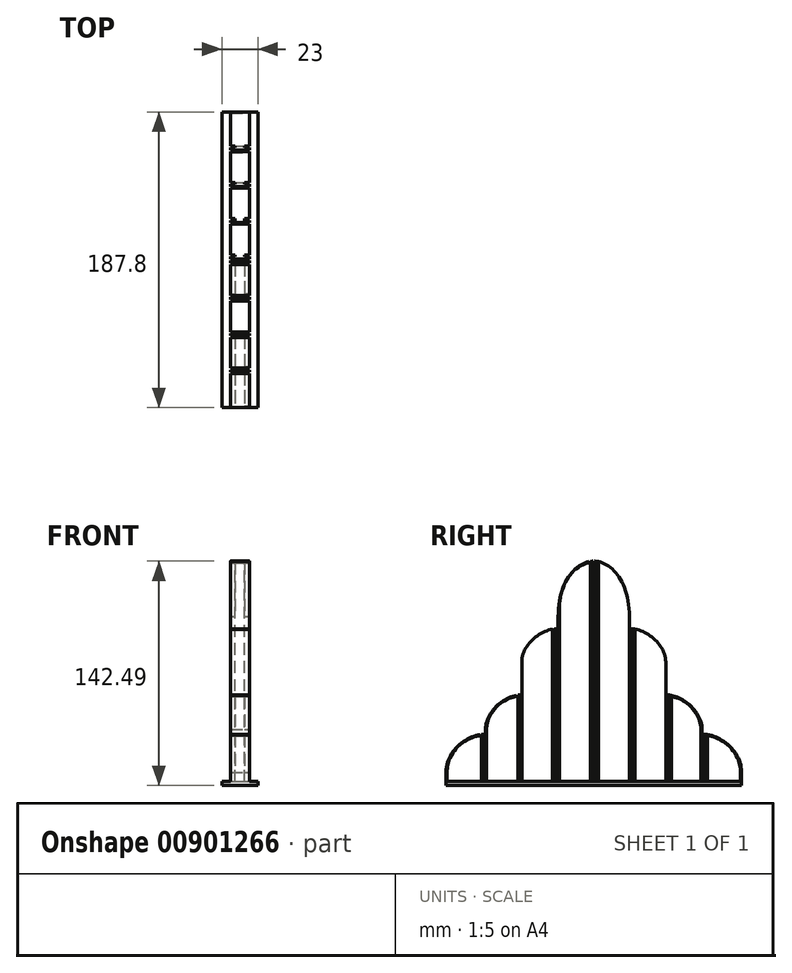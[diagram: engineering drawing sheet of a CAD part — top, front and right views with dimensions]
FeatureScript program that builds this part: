
annotation { "Feature Type Name" : "Feature", "Feature Type Description" : "" }
export const myFeature = defineFeature(function(context is Context, id is Id, definition is map)
    precondition{}
    {
        {
            var Q0;
            Q0=qCreatedBy(makeId("Right.planeOp"),FACE);
            var sketch = newSketch(context, id + "F0", { "sketchPlane" : qUnion([Q0])});
            skLineSegment(sketch, "E0", {"start": v(2, -140) * mm, "end": v(2, 0) * mm});
            skLineSegment(sketch, "E1", {"start": v(3, -140) * mm, "end": v(3, -0.3) * mm});
            skLineSegment(sketch, "E2", {"start": v(3.8, -140) * mm, "end": v(3.8, -1.32) * mm});
            skLineSegment(sketch, "E3", {"start": v(21.8, -140) * mm, "end": v(21.8, -35) * mm});
            skLineSegment(sketch, "E4", {"start": v(22.6, -140) * mm, "end": v(22.6, -35) * mm});
            skLineSegment(sketch, "E5", {"start": v(23.6, -140) * mm, "end": v(23.6, -43) * mm});
            skLineSegment(sketch, "E6", {"start": v(25.1, -140) * mm, "end": v(25.1, -43) * mm});
            skLineSegment(sketch, "E7", {"start": v(26.1, -140) * mm, "end": v(26.1, -43.2) * mm});
            skLineSegment(sketch, "E8", {"start": v(26.9, -140) * mm, "end": v(26.9, -44.15) * mm});
            skLineSegment(sketch, "E9", {"start": v(44.9, -140) * mm, "end": v(44.9, -64) * mm});
            skLineSegment(sketch, "E10", {"start": v(45.7, -140) * mm, "end": v(45.7, -64) * mm});
            skLineSegment(sketch, "E11", {"start": v(46.7, -140) * mm, "end": v(46.7, -85) * mm});
            skLineSegment(sketch, "E12", {"start": v(48.2, -140) * mm, "end": v(48.2, -85) * mm});
            skLineSegment(sketch, "E13", {"start": v(49.2, -140) * mm, "end": v(49.2, -85) * mm});
            skLineSegment(sketch, "E14", {"start": v(50, -140) * mm, "end": v(50, -86.2) * mm});
            skLineSegment(sketch, "E15", {"start": v(68, -140) * mm, "end": v(68, -107) * mm});
            skLineSegment(sketch, "E16", {"start": v(68.8, -140) * mm, "end": v(68.8, -107) * mm});
            skLineSegment(sketch, "E17", {"start": v(69.8, -140) * mm, "end": v(69.8, -110) * mm});
            skLineSegment(sketch, "E18", {"start": v(71.3, -140) * mm, "end": v(71.3, -110) * mm});
            skLineSegment(sketch, "E19", {"start": v(72.3, -140) * mm, "end": v(72.3, -110) * mm});
            skLineSegment(sketch, "E20", {"start": v(73.1, -140) * mm, "end": v(73.1, -111.15) * mm});
            skLineSegment(sketch, "E21", {"start": v(0.5, -140) * mm, "end": v(0.5, 0) * mm});
            skLineSegment(sketch, "E22", {"start": v(0, 0) * mm, "end": v(0, -140) * mm, "construction": true});
            skLineSegment(sketch, "E23", {"start": v(0, 0) * mm, "end": v(0, 21.1) * mm, "construction": true});
            skLineSegment(sketch, "E24", {"start": v(0, -140) * mm, "end": v(93.9, -140) * mm});
            skLineSegment(sketch, "E25", {"start": v(93.1, -140) * mm, "end": v(93.1, -134) * mm});
            skLineSegment(sketch, "E26", {"start": v(93.9, -140) * mm, "end": v(93.9, -134) * mm});
            skLineSegment(sketch, "E27", {"start": v(116.83, -43) * mm, "end": v(0, -43) * mm, "construction": true});
            skLineSegment(sketch, "E28", {"start": v(0, -85) * mm, "end": v(135.66, -85) * mm, "construction": true});
            skLineSegment(sketch, "E29", {"start": v(0, -110) * mm, "end": v(143.7, -110) * mm, "construction": true});
            skFitSpline(sketch, "E30", {"points": [v(69.8, -110) * mm, v(93.9, -134) * mm], "startDerivative": vector(30.93, 0) * mm, "endDerivative": vector(0, -40.3) * mm});
            skFitSpline(sketch, "E31", {"points": [v(46.7, -85) * mm, v(68.8, -107) * mm], "startDerivative": vector(29.83, 0) * mm, "endDerivative": vector(0, -33.26) * mm});
            skFitSpline(sketch, "E32", {"points": [v(23.6, -43) * mm, v(45.7, -64) * mm], "startDerivative": vector(30.98, 0) * mm, "endDerivative": vector(0, -31.98) * mm});
            skFitSpline(sketch, "E33", {"points": [v(0, 0) * mm, v(22.6, -35) * mm], "startDerivative": vector(33.21, 0) * mm, "endDerivative": vector(0, -66.82) * mm});
            skLineSegment(sketch, "E34", {"start": v(0, 0) * mm, "end": v(35.18, 0) * mm, "construction": true});
            skFitSpline(sketch, "E35.trimOffspring", {"points": [v(0, -0.8) * mm, v(1.3, -0.8) * mm, v(3.94, -1.18) * mm, v(9.13, -3.4) * mm, v(15.13, -8.92) * mm, v(20.38, -19.7) * mm, v(21.8, -29.5) * mm, v(21.8, -35) * mm]});
            skFitSpline(sketch, "E36.trimOffspring", {"points": [v(23.6, -43.8) * mm, v(26.05, -43.8) * mm, v(31.18, -45.03) * mm, v(38.3, -49.77) * mm, v(42.64, -55.32) * mm, v(44.55, -60.22) * mm, v(44.9, -62.74) * mm, v(44.9, -64) * mm]});
            skFitSpline(sketch, "E37.trimOffspring", {"points": [v(46.7, -85.8) * mm, v(47.87, -85.8) * mm, v(50.3, -86.12) * mm, v(55.27, -87.93) * mm, v(61.23, -92.08) * mm, v(65.67, -97.92) * mm, v(67.64, -103.06) * mm, v(68, -105.69) * mm, v(68, -107) * mm]});
            skFitSpline(sketch, "E38.trimOffspring", {"points": [v(69.8, -110.8) * mm, v(71.02, -110.8) * mm, v(73.59, -111.11) * mm, v(78.94, -112.91) * mm, v(85.5, -117.15) * mm, v(90.46, -123.41) * mm, v(92.69, -129.25) * mm, v(93.1, -132.39) * mm, v(93.1, -134) * mm]});
            skPoint(sketch, "E39.orphan", {"position": v(93.9, -124.2) * mm});
            skLineSegment(sketch, "E40", {"start": v(69.8, -110) * mm, "end": v(68.8, -110) * mm});
            skLineSegment(sketch, "E41", {"start": v(46.7, -85) * mm, "end": v(45.7, -85) * mm});
            skLineSegment(sketch, "E42", {"start": v(23.6, -43) * mm, "end": v(22.6, -43) * mm});
            skLineSegment(sketch, "E43.MirrorCS", {"start": v(-0.5, -140) * mm, "end": v(-0.5, 0) * mm});
            skLineSegment(sketch, "E44.MirrorCS", {"start": v(-2, -140) * mm, "end": v(-2, 0) * mm});
            skLineSegment(sketch, "E45.MirrorCS", {"start": v(-3, -140) * mm, "end": v(-3, -0.3) * mm});
            skLineSegment(sketch, "E46.MirrorCS", {"start": v(-3.8, -140) * mm, "end": v(-3.8, -1.32) * mm});
            skLineSegment(sketch, "E47.MirrorCS", {"start": v(-21.8, -140) * mm, "end": v(-21.8, -35) * mm});
            skLineSegment(sketch, "E48.MirrorCS", {"start": v(-22.6, -140) * mm, "end": v(-22.6, -35) * mm});
            skLineSegment(sketch, "E49.MirrorCS", {"start": v(-23.6, -140) * mm, "end": v(-23.6, -43) * mm});
            skLineSegment(sketch, "E50.MirrorCS", {"start": v(-25.1, -140) * mm, "end": v(-25.1, -43) * mm});
            skLineSegment(sketch, "E51.MirrorCS", {"start": v(-26.1, -140) * mm, "end": v(-26.1, -43.2) * mm});
            skLineSegment(sketch, "E52.MirrorCS", {"start": v(-26.9, -140) * mm, "end": v(-26.9, -44.15) * mm});
            skLineSegment(sketch, "E53.MirrorCS", {"start": v(-44.9, -140) * mm, "end": v(-44.9, -64) * mm});
            skLineSegment(sketch, "E54.MirrorCS", {"start": v(-45.7, -140) * mm, "end": v(-45.7, -64) * mm});
            skLineSegment(sketch, "E55.MirrorCS", {"start": v(-46.7, -140) * mm, "end": v(-46.7, -85) * mm});
            skLineSegment(sketch, "E56.MirrorCS", {"start": v(-48.2, -140) * mm, "end": v(-48.2, -85) * mm});
            skLineSegment(sketch, "E57.MirrorCS", {"start": v(-49.2, -140) * mm, "end": v(-49.2, -85) * mm});
            skLineSegment(sketch, "E58.MirrorCS", {"start": v(-50, -140) * mm, "end": v(-50, -86.2) * mm});
            skLineSegment(sketch, "E59.MirrorCS", {"start": v(-68, -140) * mm, "end": v(-68, -107) * mm});
            skLineSegment(sketch, "E60.MirrorCS", {"start": v(-68.8, -140) * mm, "end": v(-68.8, -107) * mm});
            skLineSegment(sketch, "E61.MirrorCS", {"start": v(-69.8, -140) * mm, "end": v(-69.8, -110) * mm});
            skLineSegment(sketch, "E62.MirrorCS", {"start": v(-71.3, -140) * mm, "end": v(-71.3, -110) * mm});
            skLineSegment(sketch, "E63.MirrorCS", {"start": v(-72.3, -140) * mm, "end": v(-72.3, -110) * mm});
            skLineSegment(sketch, "E64.MirrorCS", {"start": v(-73.1, -140) * mm, "end": v(-73.1, -111.15) * mm});
            skLineSegment(sketch, "E65.MirrorCS", {"start": v(-93.1, -140) * mm, "end": v(-93.1, -134) * mm});
            skLineSegment(sketch, "E66.MirrorCS", {"start": v(-93.9, -140) * mm, "end": v(-93.9, -134) * mm});
            skFitSpline(sketch, "E67.MirrorCS", {"points": [v(-69.8, -110) * mm, v(-93.9, -134) * mm], "startDerivative": vector(-30.93, 0) * mm, "endDerivative": vector(0, -40.3) * mm});
            skFitSpline(sketch, "E68.MirrorCS", {"points": [v(-46.7, -85) * mm, v(-68.8, -107) * mm], "startDerivative": vector(-29.83, 0) * mm, "endDerivative": vector(0, -33.26) * mm});
            skFitSpline(sketch, "E69.MirrorCS", {"points": [v(-23.6, -43) * mm, v(-45.7, -64) * mm], "startDerivative": vector(-30.98, 0) * mm, "endDerivative": vector(0, -31.98) * mm});
            skFitSpline(sketch, "E70.MirrorCS", {"points": [v(0, 0) * mm, v(-22.6, -35) * mm], "startDerivative": vector(-33.21, 0) * mm, "endDerivative": vector(0, -66.82) * mm});
            skFitSpline(sketch, "E71.0", {"points": [v(0, -0.8) * mm, v(-1.3, -0.8) * mm, v(-3.94, -1.18) * mm, v(-9.13, -3.4) * mm, v(-15.13, -8.92) * mm, v(-20.38, -19.7) * mm, v(-21.8, -29.5) * mm, v(-21.8, -35) * mm]});
            skFitSpline(sketch, "E72.0", {"points": [v(-23.6, -43.8) * mm, v(-26.05, -43.8) * mm, v(-31.18, -45.03) * mm, v(-38.3, -49.77) * mm, v(-42.64, -55.32) * mm, v(-44.55, -60.22) * mm, v(-44.9, -62.74) * mm, v(-44.9, -64) * mm]});
            skFitSpline(sketch, "E73.0", {"points": [v(-46.7, -85.8) * mm, v(-47.87, -85.8) * mm, v(-50.3, -86.12) * mm, v(-55.27, -87.93) * mm, v(-61.23, -92.08) * mm, v(-65.67, -97.92) * mm, v(-67.64, -103.06) * mm, v(-68, -105.69) * mm, v(-68, -107) * mm]});
            skFitSpline(sketch, "E74.0", {"points": [v(-69.8, -110.8) * mm, v(-71.02, -110.8) * mm, v(-73.59, -111.11) * mm, v(-78.94, -112.91) * mm, v(-85.5, -117.15) * mm, v(-90.46, -123.41) * mm, v(-92.69, -129.25) * mm, v(-93.1, -132.39) * mm, v(-93.1, -134) * mm]});
            skLineSegment(sketch, "E75.bottom", {"start": v(93.9, -140) * mm, "end": v(-93.9, -140) * mm});
            skLineSegment(sketch, "E75.top", {"start": v(93.9, -142.5) * mm, "end": v(-93.9, -142.5) * mm});
            skLineSegment(sketch, "E75.left", {"start": v(93.9, -140) * mm, "end": v(93.9, -142.5) * mm});
            skLineSegment(sketch, "E75.right", {"start": v(-93.9, -140) * mm, "end": v(-93.9, -142.5) * mm});
            skLineSegment(sketch, "E76", {"start": v(-69.8, -110) * mm, "end": v(-68.8, -110) * mm});
            skLineSegment(sketch, "E77", {"start": v(-46.7, -85) * mm, "end": v(-45.7, -85) * mm});
            skLineSegment(sketch, "E78", {"start": v(-23.6, -43) * mm, "end": v(-22.6, -43) * mm});
            skFitSpline(sketch, "E79.0", {"points": [v(0, -0.8) * mm, v(1.3, -0.8) * mm, v(3.94, -1.18) * mm, v(9.13, -3.4) * mm, v(15.13, -8.92) * mm, v(20.38, -19.7) * mm, v(21.8, -29.5) * mm, v(21.8, -35) * mm]});
            skLineSegment(sketch, "E80", {"start": v(-23.6, -43.8) * mm, "end": v(-22.6, -43.8) * mm});
            skLineSegment(sketch, "E81", {"start": v(-46.7, -85.8) * mm, "end": v(-45.7, -85.8) * mm});
            skLineSegment(sketch, "E82", {"start": v(-69.8, -110.8) * mm, "end": v(-68.8, -110.8) * mm});
            skFitSpline(sketch, "E83.0", {"points": [v(23.6, -43.8) * mm, v(26.05, -43.8) * mm, v(31.18, -45.03) * mm, v(38.3, -49.77) * mm, v(42.64, -55.32) * mm, v(44.55, -60.22) * mm, v(44.9, -62.74) * mm, v(44.9, -64) * mm]});
            skFitSpline(sketch, "E84.0", {"points": [v(46.7, -85.8) * mm, v(47.87, -85.8) * mm, v(50.3, -86.12) * mm, v(55.27, -87.93) * mm, v(61.23, -92.08) * mm, v(65.67, -97.92) * mm, v(67.64, -103.06) * mm, v(68, -105.69) * mm, v(68, -107) * mm]});
            skFitSpline(sketch, "E85.0", {"points": [v(69.8, -110.8) * mm, v(71.02, -110.8) * mm, v(73.59, -111.11) * mm, v(78.94, -112.91) * mm, v(85.5, -117.15) * mm, v(90.46, -123.41) * mm, v(92.69, -129.25) * mm, v(93.1, -132.39) * mm, v(93.1, -134) * mm]});
            skLineSegment(sketch, "E86", {"start": v(69.8, -110.8) * mm, "end": v(68.8, -110.8) * mm});
            skLineSegment(sketch, "E87", {"start": v(46.7, -85.8) * mm, "end": v(45.7, -85.8) * mm});
            skLineSegment(sketch, "E88", {"start": v(23.6, -43.8) * mm, "end": v(22.6, -43.8) * mm});
            skSolve(sketch);
        }
        {
            var Q0;
            {var subQ0=sQuery(id+"F0.wireOp",EDGE,"E64.MirrorCS");Q0=makeQuery(id+"F0.imprint","IMPRINT",FACE,{"disambiguationData":[TD([[makeQuery(id+"F0.imprint","IMPRINT",EDGE,{"derivedFrom":subQ0}),1.0]])]});}
            var Q1;
            {var subQ0=sQuery(id+"F0.wireOp",EDGE,"E75.bottom");var subQ1=sQuery(id+"F0.wireOp",EDGE,"E62.MirrorCS");var subQ2=makeQuery(id+"F0.imprint","INTERSECT",VERTEX,{"derivedFrom":[subQ1,subQ0]});Q1=makeQuery(id+"F0.imprint","IMPRINT",FACE,{"disambiguationData":[TD([[makeQuery(id+"F0.imprint","IMPRINT",EDGE,{"disambiguationData":[TD([[subQ2,-1.0]])],"derivedFrom":subQ1}),1.0]])]});}
            var Q2;
            {var subQ0=sQuery(id+"F0.wireOp",EDGE,"E58.MirrorCS");Q2=makeQuery(id+"F0.imprint","IMPRINT",FACE,{"disambiguationData":[TD([[makeQuery(id+"F0.imprint","IMPRINT",EDGE,{"derivedFrom":subQ0}),1.0]])]});}
            var Q3;
            {var subQ0=sQuery(id+"F0.wireOp",EDGE,"E75.bottom");var subQ1=sQuery(id+"F0.wireOp",EDGE,"E56.MirrorCS");var subQ2=makeQuery(id+"F0.imprint","INTERSECT",VERTEX,{"derivedFrom":[subQ1,subQ0]});Q3=makeQuery(id+"F0.imprint","IMPRINT",FACE,{"disambiguationData":[TD([[makeQuery(id+"F0.imprint","IMPRINT",EDGE,{"disambiguationData":[TD([[subQ2,-1.0]])],"derivedFrom":subQ1}),1.0]])]});}
            var Q4;
            {var subQ5=sQuery(id+"F0.wireOp",EDGE,"E53.MirrorCS");Q4=makeQuery(id+"F0.imprint","IMPRINT",FACE,{"disambiguationData":[TD([[makeQuery(id+"F0.imprint","IMPRINT",EDGE,{"derivedFrom":subQ5}),-1.0]])]});}
            var Q5;
            {var subQ0=sQuery(id+"F0.wireOp",EDGE,"E75.bottom");var subQ1=sQuery(id+"F0.wireOp",EDGE,"E50.MirrorCS");var subQ2=makeQuery(id+"F0.imprint","INTERSECT",VERTEX,{"derivedFrom":[subQ1,subQ0]});Q5=makeQuery(id+"F0.imprint","IMPRINT",FACE,{"disambiguationData":[TD([[makeQuery(id+"F0.imprint","IMPRINT",EDGE,{"disambiguationData":[TD([[subQ2,-1.0]])],"derivedFrom":subQ1}),1.0]])]});}
            var Q6;
            {var subQ0=sQuery(id+"F0.wireOp",EDGE,"E46.MirrorCS");Q6=makeQuery(id+"F0.imprint","IMPRINT",FACE,{"disambiguationData":[TD([[makeQuery(id+"F0.imprint","IMPRINT",EDGE,{"derivedFrom":subQ0}),1.0]])]});}
            var Q7;
            {var subQ0=sQuery(id+"F0.wireOp",EDGE,"E75.bottom");var subQ1=sQuery(id+"F0.wireOp",EDGE,"E44.MirrorCS");var subQ2=makeQuery(id+"F0.imprint","INTERSECT",VERTEX,{"derivedFrom":[subQ1,subQ0]});Q7=makeQuery(id+"F0.imprint","IMPRINT",FACE,{"disambiguationData":[TD([[makeQuery(id+"F0.imprint","IMPRINT",EDGE,{"disambiguationData":[TD([[subQ2,-1.0]])],"derivedFrom":subQ1}),1.0]])]});}
            var Q8;
            {var subQ4=sQuery(id+"F0.wireOp",EDGE,"E75.bottom");var subQ11=makeQuery(id+"F0.imprint","IMPRINT",VERTEX,{"derivedFrom":subQ4});Q8=makeQuery(id+"F0.imprint","IMPRINT",FACE,{"disambiguationData":[TD([[makeQuery(id+"F0.imprint","IMPRINT",EDGE,{"disambiguationData":[TD([[subQ11,1.0]])],"derivedFrom":subQ4}),-1.0]])]});}
            var Q9;
            {var subQ0=sQuery(id+"F0.wireOp",EDGE,"E2");Q9=makeQuery(id+"F0.imprint","IMPRINT",FACE,{"disambiguationData":[TD([[makeQuery(id+"F0.imprint","IMPRINT",EDGE,{"derivedFrom":subQ0}),-1.0]])]});}
            var Q10;
            {var subQ4=sQuery(id+"F0.wireOp",EDGE,"E9");Q10=makeQuery(id+"F0.imprint","IMPRINT",FACE,{"disambiguationData":[TD([[makeQuery(id+"F0.imprint","IMPRINT",EDGE,{"derivedFrom":subQ4}),1.0]])]});}
            var Q11;
            {var subQ0=sQuery(id+"F0.wireOp",EDGE,"E75.bottom");var subQ1=sQuery(id+"F0.wireOp",EDGE,"E12");var subQ2=makeQuery(id+"F0.imprint","INTERSECT",VERTEX,{"derivedFrom":[subQ1,subQ0]});Q11=makeQuery(id+"F0.imprint","IMPRINT",FACE,{"disambiguationData":[TD([[makeQuery(id+"F0.imprint","IMPRINT",EDGE,{"disambiguationData":[TD([[subQ2,-1.0]])],"derivedFrom":subQ1}),-1.0]])]});}
            var Q12;
            {var subQ0=sQuery(id+"F0.wireOp",EDGE,"E14");Q12=makeQuery(id+"F0.imprint","IMPRINT",FACE,{"disambiguationData":[TD([[makeQuery(id+"F0.imprint","IMPRINT",EDGE,{"derivedFrom":subQ0}),-1.0]])]});}
            var Q13;
            {var subQ0=sQuery(id+"F0.wireOp",EDGE,"E75.bottom");var subQ1=sQuery(id+"F0.wireOp",EDGE,"E18");var subQ2=makeQuery(id+"F0.imprint","INTERSECT",VERTEX,{"derivedFrom":[subQ1,subQ0]});Q13=makeQuery(id+"F0.imprint","IMPRINT",FACE,{"disambiguationData":[TD([[makeQuery(id+"F0.imprint","IMPRINT",EDGE,{"disambiguationData":[TD([[subQ2,-1.0]])],"derivedFrom":subQ1}),-1.0]])]});}
            var Q14;
            {var subQ0=sQuery(id+"F0.wireOp",EDGE,"E20");Q14=makeQuery(id+"F0.imprint","IMPRINT",FACE,{"disambiguationData":[TD([[makeQuery(id+"F0.imprint","IMPRINT",EDGE,{"derivedFrom":subQ0}),-1.0]])]});}
            var Q15;
            {var subQ0=sQuery(id+"F0.wireOp",EDGE,"E75.bottom");var subQ1=sQuery(id+"F0.wireOp",EDGE,"E0");var subQ2=makeQuery(id+"F0.imprint","INTERSECT",VERTEX,{"derivedFrom":[subQ1,subQ0]});Q15=makeQuery(id+"F0.imprint","IMPRINT",FACE,{"disambiguationData":[TD([[makeQuery(id+"F0.imprint","IMPRINT",EDGE,{"disambiguationData":[TD([[subQ2,-1.0]])],"derivedFrom":subQ1}),-1.0]])]});}
            var Q16;
            {var subQ3=sQuery(id+"F0.wireOp",EDGE,"E80");Q16=makeQuery(id+"F0.imprint","IMPRINT",FACE,{"disambiguationData":[TD([[makeQuery(id+"F0.imprint","IMPRINT",EDGE,{"derivedFrom":subQ3}),-1.0]])]});}
            var Q17;
            {var subQ3=sQuery(id+"F0.wireOp",EDGE,"E81");Q17=makeQuery(id+"F0.imprint","IMPRINT",FACE,{"disambiguationData":[TD([[makeQuery(id+"F0.imprint","IMPRINT",EDGE,{"derivedFrom":subQ3}),-1.0]])]});}
            var Q18;
            {var subQ3=sQuery(id+"F0.wireOp",EDGE,"E82");Q18=makeQuery(id+"F0.imprint","IMPRINT",FACE,{"disambiguationData":[TD([[makeQuery(id+"F0.imprint","IMPRINT",EDGE,{"derivedFrom":subQ3}),-1.0]])]});}
            var Q19;
            {var subQ0=sQuery(id+"F0.wireOp",EDGE,"E75.bottom");var subQ1=sQuery(id+"F0.wireOp",EDGE,"E6");var subQ2=makeQuery(id+"F0.imprint","INTERSECT",VERTEX,{"derivedFrom":[subQ1,subQ0]});Q19=makeQuery(id+"F0.imprint","IMPRINT",FACE,{"disambiguationData":[TD([[makeQuery(id+"F0.imprint","IMPRINT",EDGE,{"disambiguationData":[TD([[subQ2,-1.0]])],"derivedFrom":subQ1}),-1.0]])]});}
            var Q20;
            {var subQ3=sQuery(id+"F0.wireOp",EDGE,"E88");Q20=makeQuery(id+"F0.imprint","IMPRINT",FACE,{"disambiguationData":[TD([[makeQuery(id+"F0.imprint","IMPRINT",EDGE,{"derivedFrom":subQ3}),1.0]])]});}
            var Q21;
            {var subQ3=sQuery(id+"F0.wireOp",EDGE,"E87");Q21=makeQuery(id+"F0.imprint","IMPRINT",FACE,{"disambiguationData":[TD([[makeQuery(id+"F0.imprint","IMPRINT",EDGE,{"derivedFrom":subQ3}),1.0]])]});}
            var Q22;
            {var subQ3=sQuery(id+"F0.wireOp",EDGE,"E86");Q22=makeQuery(id+"F0.imprint","IMPRINT",FACE,{"disambiguationData":[TD([[makeQuery(id+"F0.imprint","IMPRINT",EDGE,{"derivedFrom":subQ3}),1.0]])]});}
            extrude(context, id + "F1", {"entities" : qUnion([Q0, Q1, Q2, Q3, Q4, Q5, Q6, Q7, Q8, Q9, Q10, Q11, Q12, Q13, Q14, Q15, Q16, Q17, Q18, Q19, Q20, Q21, Q22]), "oppositeDirection" : true, "depth" : 6 * mm, "offsetDistance" : 25 * mm, "symmetric" : true});
        }
        {
            var Q0;
            {var subQ5=sQuery(id+"F0.wireOp",EDGE,"E65.MirrorCS");Q0=makeQuery(id+"F0.imprint","IMPRINT",FACE,{"disambiguationData":[TD([[makeQuery(id+"F0.imprint","IMPRINT",EDGE,{"derivedFrom":subQ5}),1.0]])]});}
            var Q1;
            {var subQ5=sQuery(id+"F0.wireOp",EDGE,"E64.MirrorCS");Q1=makeQuery(id+"F0.imprint","IMPRINT",FACE,{"disambiguationData":[TD([[makeQuery(id+"F0.imprint","IMPRINT",EDGE,{"derivedFrom":subQ5}),-1.0]])]});}
            var Q2;
            {var subQ0=sQuery(id+"F0.wireOp",EDGE,"E75.bottom");var subQ1=sQuery(id+"F0.wireOp",EDGE,"E61.MirrorCS");var subQ2=makeQuery(id+"F0.imprint","INTERSECT",VERTEX,{"derivedFrom":[subQ1,subQ0]});Q2=makeQuery(id+"F0.imprint","IMPRINT",FACE,{"disambiguationData":[TD([[makeQuery(id+"F0.imprint","IMPRINT",EDGE,{"disambiguationData":[TD([[subQ2,-1.0]])],"derivedFrom":subQ1}),1.0]])]});}
            var Q3;
            {var subQ0=sQuery(id+"F0.wireOp",EDGE,"E67.MirrorCS");var subQ5=sQuery(id+"F0.wireOp",EDGE,"E62.MirrorCS");var subQ6=makeQuery(id+"F0.imprint","INTERSECT",VERTEX,{"derivedFrom":[subQ5,subQ0]});Q3=makeQuery(id+"F0.imprint","IMPRINT",FACE,{"disambiguationData":[TD([[makeQuery(id+"F0.imprint","IMPRINT",EDGE,{"disambiguationData":[TD([[subQ6,1.0]])],"derivedFrom":subQ5}),-1.0]])]});}
            var Q4;
            {var subQ10=sQuery(id+"F0.wireOp",EDGE,"E59.MirrorCS");Q4=makeQuery(id+"F0.imprint","IMPRINT",FACE,{"disambiguationData":[TD([[makeQuery(id+"F0.imprint","IMPRINT",EDGE,{"derivedFrom":subQ10}),1.0]])]});}
            var Q5;
            {var subQ5=sQuery(id+"F0.wireOp",EDGE,"E58.MirrorCS");Q5=makeQuery(id+"F0.imprint","IMPRINT",FACE,{"disambiguationData":[TD([[makeQuery(id+"F0.imprint","IMPRINT",EDGE,{"derivedFrom":subQ5}),-1.0]])]});}
            var Q6;
            {var subQ0=sQuery(id+"F0.wireOp",EDGE,"E75.bottom");var subQ1=sQuery(id+"F0.wireOp",EDGE,"E55.MirrorCS");var subQ2=makeQuery(id+"F0.imprint","INTERSECT",VERTEX,{"derivedFrom":[subQ1,subQ0]});Q6=makeQuery(id+"F0.imprint","IMPRINT",FACE,{"disambiguationData":[TD([[makeQuery(id+"F0.imprint","IMPRINT",EDGE,{"disambiguationData":[TD([[subQ2,-1.0]])],"derivedFrom":subQ1}),1.0]])]});}
            var Q7;
            {var subQ6=sQuery(id+"F0.wireOp",EDGE,"E53.MirrorCS");Q7=makeQuery(id+"F0.imprint","IMPRINT",FACE,{"disambiguationData":[TD([[makeQuery(id+"F0.imprint","IMPRINT",EDGE,{"derivedFrom":subQ6}),1.0]])]});}
            var Q8;
            {var subQ0=sQuery(id+"F0.wireOp",EDGE,"E68.MirrorCS");var subQ5=sQuery(id+"F0.wireOp",EDGE,"E56.MirrorCS");var subQ6=makeQuery(id+"F0.imprint","INTERSECT",VERTEX,{"derivedFrom":[subQ5,subQ0]});Q8=makeQuery(id+"F0.imprint","IMPRINT",FACE,{"disambiguationData":[TD([[makeQuery(id+"F0.imprint","IMPRINT",EDGE,{"disambiguationData":[TD([[subQ6,1.0]])],"derivedFrom":subQ5}),-1.0]])]});}
            var Q9;
            {var subQ5=sQuery(id+"F0.wireOp",EDGE,"E47.MirrorCS");Q9=makeQuery(id+"F0.imprint","IMPRINT",FACE,{"disambiguationData":[TD([[makeQuery(id+"F0.imprint","IMPRINT",EDGE,{"derivedFrom":subQ5}),1.0]])]});}
            var Q10;
            {var subQ0=sQuery(id+"F0.wireOp",EDGE,"E75.bottom");var subQ1=sQuery(id+"F0.wireOp",EDGE,"E49.MirrorCS");var subQ2=makeQuery(id+"F0.imprint","INTERSECT",VERTEX,{"derivedFrom":[subQ1,subQ0]});Q10=makeQuery(id+"F0.imprint","IMPRINT",FACE,{"disambiguationData":[TD([[makeQuery(id+"F0.imprint","IMPRINT",EDGE,{"disambiguationData":[TD([[subQ2,-1.0]])],"derivedFrom":subQ1}),1.0]])]});}
            var Q11;
            {var subQ0=sQuery(id+"F0.wireOp",EDGE,"E69.MirrorCS");var subQ5=sQuery(id+"F0.wireOp",EDGE,"E50.MirrorCS");var subQ7=makeQuery(id+"F0.imprint","INTERSECT",VERTEX,{"derivedFrom":[subQ5,subQ0]});Q11=makeQuery(id+"F0.imprint","IMPRINT",FACE,{"disambiguationData":[TD([[makeQuery(id+"F0.imprint","IMPRINT",EDGE,{"disambiguationData":[TD([[subQ7,1.0]])],"derivedFrom":subQ5}),-1.0]])]});}
            var Q12;
            {var subQ0=sQuery(id+"F0.wireOp",EDGE,"E75.bottom");var subQ1=sQuery(id+"F0.wireOp",EDGE,"E51.MirrorCS");var subQ2=makeQuery(id+"F0.imprint","INTERSECT",VERTEX,{"derivedFrom":[subQ1,subQ0]});Q12=makeQuery(id+"F0.imprint","IMPRINT",FACE,{"disambiguationData":[TD([[makeQuery(id+"F0.imprint","IMPRINT",EDGE,{"disambiguationData":[TD([[subQ2,-1.0]])],"derivedFrom":subQ1}),1.0]])]});}
            var Q13;
            {var subQ5=sQuery(id+"F0.wireOp",EDGE,"E46.MirrorCS");Q13=makeQuery(id+"F0.imprint","IMPRINT",FACE,{"disambiguationData":[TD([[makeQuery(id+"F0.imprint","IMPRINT",EDGE,{"derivedFrom":subQ5}),-1.0]])]});}
            var Q14;
            {var subQ0=sQuery(id+"F0.wireOp",EDGE,"E75.bottom");var subQ1=sQuery(id+"F0.wireOp",EDGE,"E43.MirrorCS");var subQ2=makeQuery(id+"F0.imprint","INTERSECT",VERTEX,{"derivedFrom":[subQ1,subQ0]});Q14=makeQuery(id+"F0.imprint","IMPRINT",FACE,{"disambiguationData":[TD([[makeQuery(id+"F0.imprint","IMPRINT",EDGE,{"disambiguationData":[TD([[subQ2,-1.0]])],"derivedFrom":subQ1}),1.0]])]});}
            var Q15;
            {var subQ0=sQuery(id+"F0.wireOp",EDGE,"E70.MirrorCS");var subQ1=sQuery(id+"F0.wireOp",EDGE,"E43.MirrorCS");var subQ2=makeQuery(id+"F0.imprint","INTERSECT",VERTEX,{"derivedFrom":[subQ1,subQ0]});Q15=makeQuery(id+"F0.imprint","IMPRINT",FACE,{"disambiguationData":[TD([[makeQuery(id+"F0.imprint","IMPRINT",EDGE,{"disambiguationData":[TD([[subQ2,1.0]])],"derivedFrom":subQ1}),1.0]])]});}
            var Q16;
            {var subQ0=sQuery(id+"F0.wireOp",EDGE,"E75.bottom");var subQ1=sQuery(id+"F0.wireOp",EDGE,"E0");var subQ2=makeQuery(id+"F0.imprint","INTERSECT",VERTEX,{"derivedFrom":[subQ1,subQ0]});Q16=makeQuery(id+"F0.imprint","IMPRINT",FACE,{"disambiguationData":[TD([[makeQuery(id+"F0.imprint","IMPRINT",EDGE,{"disambiguationData":[TD([[subQ2,-1.0]])],"derivedFrom":subQ1}),1.0]])]});}
            var Q17;
            {var subQ5=sQuery(id+"F0.wireOp",EDGE,"E1");Q17=makeQuery(id+"F0.imprint","IMPRINT",FACE,{"disambiguationData":[TD([[makeQuery(id+"F0.imprint","IMPRINT",EDGE,{"derivedFrom":subQ5}),-1.0]])]});}
            var Q18;
            {var subQ0=sQuery(id+"F0.wireOp",EDGE,"E5");Q18=makeQuery(id+"F0.imprint","IMPRINT",FACE,{"disambiguationData":[TD([[makeQuery(id+"F0.imprint","IMPRINT",EDGE,{"derivedFrom":subQ0}),-1.0]])]});}
            var Q19;
            {var subQ8=sQuery(id+"F0.wireOp",EDGE,"E7");Q19=makeQuery(id+"F0.imprint","IMPRINT",FACE,{"disambiguationData":[TD([[makeQuery(id+"F0.imprint","IMPRINT",EDGE,{"derivedFrom":subQ8}),-1.0]])]});}
            var Q20;
            {var subQ0=sQuery(id+"F0.wireOp",EDGE,"E11");Q20=makeQuery(id+"F0.imprint","IMPRINT",FACE,{"disambiguationData":[TD([[makeQuery(id+"F0.imprint","IMPRINT",EDGE,{"derivedFrom":subQ0}),-1.0]])]});}
            var Q21;
            {var subQ5=sQuery(id+"F0.wireOp",EDGE,"E14");Q21=makeQuery(id+"F0.imprint","IMPRINT",FACE,{"disambiguationData":[TD([[makeQuery(id+"F0.imprint","IMPRINT",EDGE,{"derivedFrom":subQ5}),1.0]])]});}
            var Q22;
            {var subQ0=sQuery(id+"F0.wireOp",EDGE,"E17");Q22=makeQuery(id+"F0.imprint","IMPRINT",FACE,{"disambiguationData":[TD([[makeQuery(id+"F0.imprint","IMPRINT",EDGE,{"derivedFrom":subQ0}),-1.0]])]});}
            var Q23;
            {var subQ2=sQuery(id+"F0.wireOp",EDGE,"E20");Q23=makeQuery(id+"F0.imprint","IMPRINT",FACE,{"disambiguationData":[TD([[makeQuery(id+"F0.imprint","IMPRINT",EDGE,{"derivedFrom":subQ2}),1.0]])]});}
            var Q24;
            {var subQ4=sQuery(id+"F0.wireOp",EDGE,"E25");Q24=makeQuery(id+"F0.imprint","IMPRINT",FACE,{"disambiguationData":[TD([[makeQuery(id+"F0.imprint","IMPRINT",EDGE,{"derivedFrom":subQ4}),-1.0]])]});}
            var Q25;
            {var subQ5=sQuery(id+"F0.wireOp",EDGE,"E15");Q25=makeQuery(id+"F0.imprint","IMPRINT",FACE,{"disambiguationData":[TD([[makeQuery(id+"F0.imprint","IMPRINT",EDGE,{"derivedFrom":subQ5}),-1.0]])]});}
            var Q26;
            {var subQ12=sQuery(id+"F0.wireOp",EDGE,"E9");Q26=makeQuery(id+"F0.imprint","IMPRINT",FACE,{"disambiguationData":[TD([[makeQuery(id+"F0.imprint","IMPRINT",EDGE,{"derivedFrom":subQ12}),-1.0]])]});}
            var Q27;
            {var subQ5=sQuery(id+"F0.wireOp",EDGE,"E3");Q27=makeQuery(id+"F0.imprint","IMPRINT",FACE,{"disambiguationData":[TD([[makeQuery(id+"F0.imprint","IMPRINT",EDGE,{"derivedFrom":subQ5}),-1.0]])]});}
            var Q28;
            {var subQ0=sQuery(id+"F0.wireOp",EDGE,"E33");var subQ1=sQuery(id+"F0.wireOp",EDGE,"E0");var subQ2=makeQuery(id+"F0.imprint","INTERSECT",VERTEX,{"derivedFrom":[subQ1,subQ0]});Q28=makeQuery(id+"F0.imprint","IMPRINT",FACE,{"disambiguationData":[TD([[makeQuery(id+"F0.imprint","IMPRINT",EDGE,{"disambiguationData":[TD([[subQ2,1.0]])],"derivedFrom":subQ1}),1.0]])]});}
            extrude(context, id + "F2", {"entities" : qUnion([Q0, Q1, Q2, Q3, Q4, Q5, Q6, Q7, Q8, Q9, Q10, Q11, Q12, Q13, Q14, Q15, Q16, Q17, Q18, Q19, Q20, Q21, Q22, Q23, Q24, Q25, Q26, Q27, Q28]), "oppositeDirection" : true, "depth" : 12 * mm, "offsetDistance" : 25 * mm, "symmetric" : true});
        }
        {
            var Q0;
            Q0=makeQuery(id+"F0.imprint","IMPRINT",FACE,{"disambiguationData":[TD([[makeQuery(id+"F0.imprint","IMPRINT",EDGE,{"derivedFrom":sQuery(id+"F0.wireOp",EDGE,"E75.top")}),-1.0]])]});
            extrude(context, id + "F3", {"entities" : qUnion([Q0]), "operationType" : NewBodyOperationType.ADD, "oppositeDirection" : true, "depth" : 23 * mm, "offsetDistance" : 25 * mm, "symmetric" : true});
        }
    });
